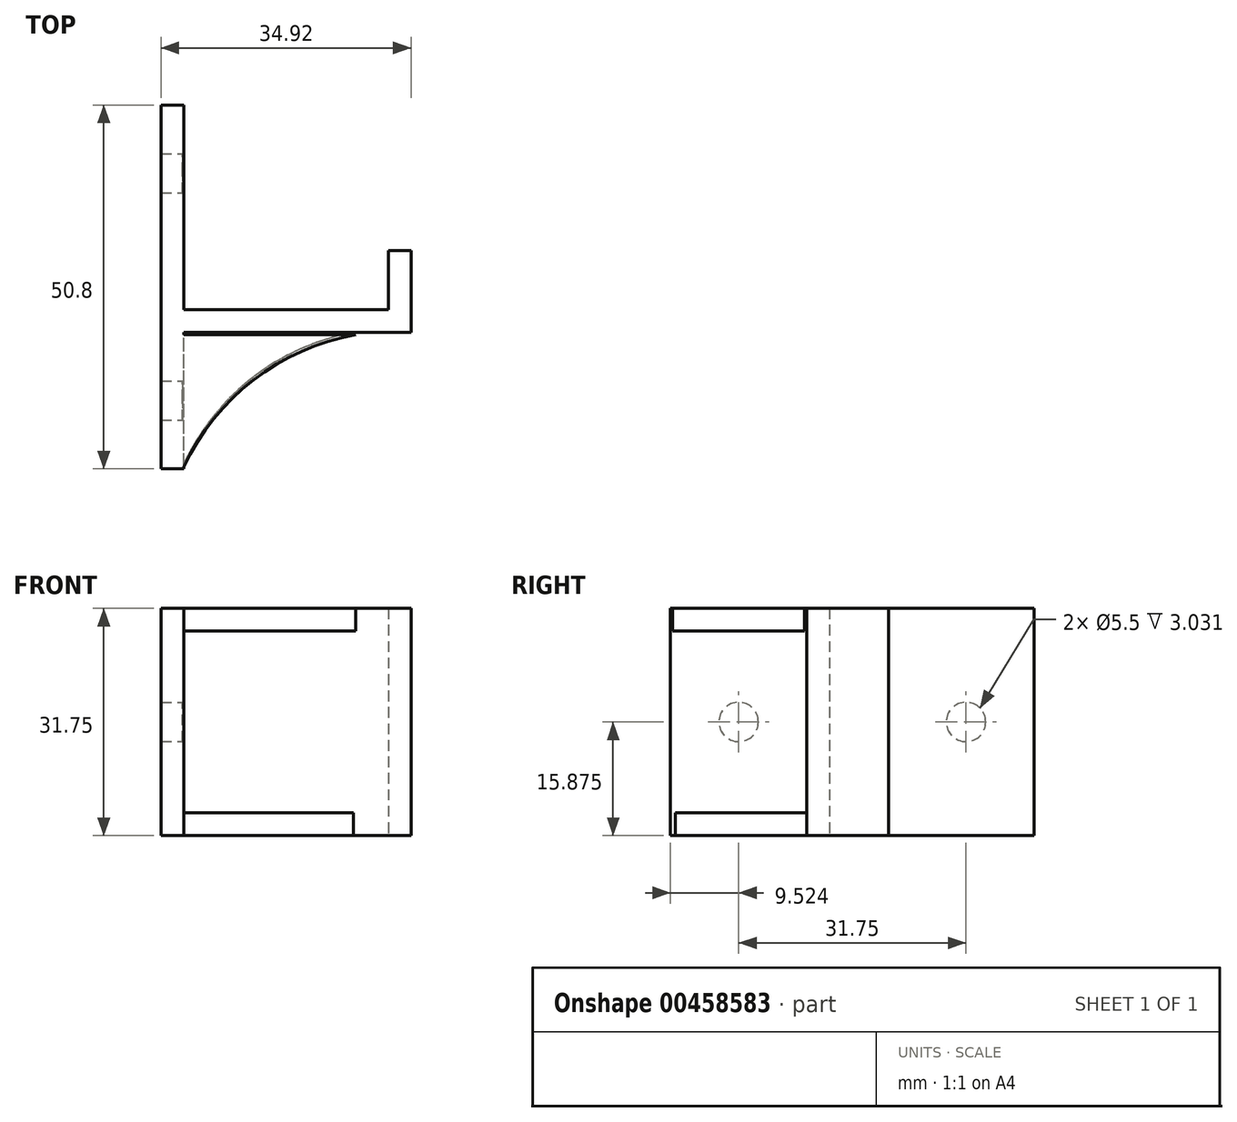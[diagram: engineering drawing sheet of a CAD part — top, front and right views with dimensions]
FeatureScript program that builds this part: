
annotation { "Feature Type Name" : "Feature", "Feature Type Description" : "" }
export const myFeature = defineFeature(function(context is Context, id is Id, definition is map)
    precondition{}
    {
        {
            var Q0;
            Q0=qCreatedBy(makeId("Top.planeOp"),FACE);
            var sketch = newSketch(context, id + "F0", { "sketchPlane" : qUnion([Q0])});
            skLineSegment(sketch, "E0", {"start": v(-3.03, 44.45) * mm, "end": v(-3.03, -6.35) * mm});
            skLineSegment(sketch, "E1", {"start": v(-3.03, -6.35) * mm, "end": v(0.14, -6.35) * mm});
            skLineSegment(sketch, "E2", {"start": v(0.14, -6.35) * mm, "end": v(0.14, 12.7) * mm});
            skLineSegment(sketch, "E3", {"start": v(0.14, 12.7) * mm, "end": v(31.9, 12.7) * mm});
            skLineSegment(sketch, "E4", {"start": v(31.9, 12.7) * mm, "end": v(31.9, 24.13) * mm});
            skLineSegment(sketch, "E5", {"start": v(31.9, 24.13) * mm, "end": v(28.72, 24.13) * mm});
            skLineSegment(sketch, "E6", {"start": v(28.72, 15.87) * mm, "end": v(0.14, 15.87) * mm});
            skLineSegment(sketch, "E7", {"start": v(0.14, 15.87) * mm, "end": v(0.14, 44.45) * mm});
            skLineSegment(sketch, "E8", {"start": v(0.14, 44.45) * mm, "end": v(-3.03, 44.45) * mm});
            skLineSegment(sketch, "E9", {"start": v(28.72, 24.13) * mm, "end": v(28.72, 15.87) * mm});
            skSolve(sketch);
        }
        {
            var Q0;
            Q0 = qSketchRegion(id + "F0", true);
            extrude(context, id + "F1", {"entities" : qUnion([Q0]), "depth" : 31.75 * mm});
        }
        {
            var Q0;
            Q0=qCreatedBy(makeId("Top.planeOp"),FACE);
            var sketch = newSketch(context, id + "F2", { "sketchPlane" : qUnion([Q0])});
            skArc(sketch, "E10", {"start": v(24.11, 12.75) * mm, "mid": v(9.75, 6.36) * mm, "end": v(0, -5.97) * mm});
            skLineSegment(sketch, "E11", {"start": v(24.11, 12.75) * mm, "end": v(0, 12.75) * mm});
            skLineSegment(sketch, "E12", {"start": v(0, 12.75) * mm, "end": v(0, -5.97) * mm});
            skSolve(sketch);
        }
        {
            var Q0;
            Q0=makeQuery(id+"F2.imprint","IMPRINT",FACE,{"disambiguationData":[TD([[makeQuery(id+"F2.imprint","IMPRINT",EDGE,{"derivedFrom":sQuery(id+"F2.wireOp",EDGE,"E10")}),-1.0]])]});
            extrude(context, id + "F3", {"entities" : qUnion([Q0]), "operationType" : NewBodyOperationType.ADD, "depth" : 3.17 * mm});
        }
        {
            var Q0;
            Q0=makeQuery(id+"F1.opExtrude","CAP_FACE",FACE,{"disambiguationData":[OSD([sQuery(id+"F0.wireOp",EDGE,"E0"),sQuery(id+"F0.wireOp",EDGE,"E1"),sQuery(id+"F0.wireOp",EDGE,"E2"),sQuery(id+"F0.wireOp",EDGE,"E3"),sQuery(id+"F0.wireOp",EDGE,"E4"),sQuery(id+"F0.wireOp",EDGE,"E5"),sQuery(id+"F0.wireOp",EDGE,"E6"),sQuery(id+"F0.wireOp",EDGE,"E7"),sQuery(id+"F0.wireOp",EDGE,"E8"),sQuery(id+"F0.wireOp",EDGE,"E9")])],"isStart":false});
            var sketch = newSketch(context, id + "F4", { "sketchPlane" : qUnion([Q0])});
            skArc(sketch, "E13", {"start": v(24.13, 12.37) * mm, "mid": v(9.77, 5.98) * mm, "end": v(0.02, -6.35) * mm});
            skLineSegment(sketch, "E14", {"start": v(24.13, 12.37) * mm, "end": v(0.02, 12.37) * mm});
            skLineSegment(sketch, "E15", {"start": v(0.02, 23.05) * mm, "end": v(0.02, 4.33) * mm});
            skSolve(sketch);
        }
        {
            var Q0;
            {var subQ0=sQuery(id+"F4.wireOp",EDGE,"E14");var subQ1=sQuery(id+"F4.wireOp",EDGE,"E13");var subQ2=makeQuery(id+"F4.imprint","INTERSECT",VERTEX,{"derivedFrom":[subQ1,subQ0]});Q0=makeQuery(id+"F4.imprint","IMPRINT",FACE,{"disambiguationData":[TD([[makeQuery(id+"F4.imprint","IMPRINT",EDGE,{"disambiguationData":[TD([[subQ2,-1.0]])],"derivedFrom":subQ1}),-1.0]])]});}
            extrude(context, id + "F5", {"entities" : qUnion([Q0]), "operationType" : NewBodyOperationType.ADD, "oppositeDirection" : true, "depth" : 3.17 * mm});
        }
        {
            var Q0;
            Q0=qCreatedBy(makeId("Right.planeOp"),FACE);
            var sketch = newSketch(context, id + "F6", { "sketchPlane" : qUnion([Q0])});
            skCircle(sketch, "E16", {"center": v(3.17, 15.88) * mm, "radius": 2.22 * mm});
            skCircle(sketch, "E17", {"center": v(34.92, 15.88) * mm, "radius": 2.22 * mm});
            skSolve(sketch);
        }
        {
            var Q0;
            Q0=sQuery(id+"F6.wireOp",VERTEX,"E16.center");
            var Q1;
            Q1=sQuery(id+"F6.wireOp",VERTEX,"E17.center");
            var Q2;
            Q2=makeQuery(id+"F1.opExtrude","SWEPT_BODY",BODY,{"disambiguationData":[OSD([sQuery(id+"F0.wireOp",EDGE,"E0"),sQuery(id+"F0.wireOp",EDGE,"E1"),sQuery(id+"F0.wireOp",EDGE,"E2"),sQuery(id+"F0.wireOp",EDGE,"E3"),sQuery(id+"F0.wireOp",EDGE,"E4"),sQuery(id+"F0.wireOp",EDGE,"E5"),sQuery(id+"F0.wireOp",EDGE,"E6"),sQuery(id+"F0.wireOp",EDGE,"E7"),sQuery(id+"F0.wireOp",EDGE,"E8"),sQuery(id+"F0.wireOp",EDGE,"E9")])]});
            hole(context, id + "F7", {"style" : HoleStyle.SIMPLE, "endStyle" : HoleEndStyle.THROUGH, "holeDiameter" : 5.5 * mm, "isTappedThrough" : true, "tappedDepth" : 12.7 * mm, "tapClearance" : 3, "startFromSketch" : true, "locations" : qUnion([Q0, Q1]), "scope" : qUnion([Q2])});
        }
    });
